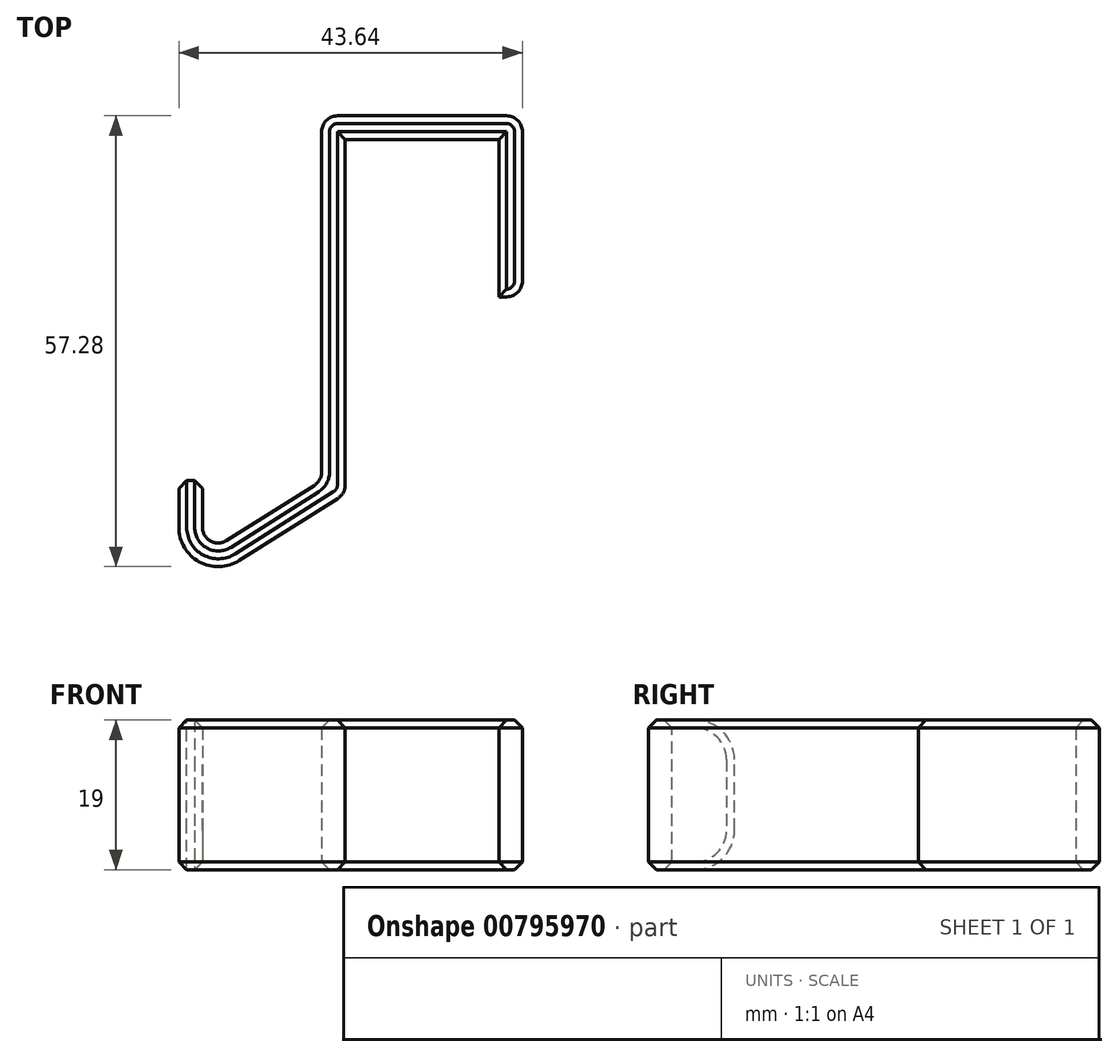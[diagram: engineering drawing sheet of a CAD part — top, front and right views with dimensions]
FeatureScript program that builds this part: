
annotation { "Feature Type Name" : "Feature", "Feature Type Description" : "" }
export const myFeature = defineFeature(function(context is Context, id is Id, definition is map)
    precondition{}
    {
        {
            var Q0;
            Q0=qCreatedBy(makeId("Top.planeOp"),FACE);
            var sketch = newSketch(context, id + "F0", { "sketchPlane" : qUnion([Q0])});
            skLineSegment(sketch, "E0", {"start": v(0, 0) * mm, "end": v(0, -15) * mm});
            skLineSegment(sketch, "E1", {"start": v(0, -15) * mm, "end": v(21.14, -1.65) * mm});
            skLineSegment(sketch, "E2", {"start": v(21.14, -1.65) * mm, "end": v(21.14, 43.35) * mm});
            skLineSegment(sketch, "E3", {"start": v(21.14, 43.35) * mm, "end": v(40.64, 43.35) * mm});
            skLineSegment(sketch, "E4", {"start": v(40.64, 43.35) * mm, "end": v(40.64, 23.35) * mm});
            skLineSegment(sketch, "E5", {"start": v(40.64, 23.35) * mm, "end": v(43.64, 23.35) * mm});
            skLineSegment(sketch, "E6", {"start": v(43.64, 23.35) * mm, "end": v(43.64, 46.35) * mm});
            skLineSegment(sketch, "E7", {"start": v(43.64, 46.35) * mm, "end": v(18.14, 46.35) * mm});
            skLineSegment(sketch, "E8", {"start": v(18.14, 46.35) * mm, "end": v(18.14, 0) * mm});
            skLineSegment(sketch, "E9", {"start": v(18.14, 0) * mm, "end": v(3, -9.56) * mm});
            skLineSegment(sketch, "E10", {"start": v(3, -9.56) * mm, "end": v(3, 0) * mm});
            skLineSegment(sketch, "E11", {"start": v(3, 0) * mm, "end": v(0, 0) * mm});
            skSolve(sketch);
        }
        {
            var Q0;
            Q0=makeQuery(id+"F0.imprint","IMPRINT",FACE,{"disambiguationData":[TD([[makeQuery(id+"F0.imprint","IMPRINT",EDGE,{"derivedFrom":sQuery(id+"F0.wireOp",EDGE,"E0")}),1.0]])]});
            extrude(context, id + "F1", {"entities" : qUnion([Q0]), "depth" : 19 * mm, "offsetDistance" : 25 * mm});
        }
        {
            var Q0;
            Q0=makeQuery(id+"F1.opExtrude","CAP_EDGE",EDGE,{"disambiguationData":[OSD([sQuery(id+"F0.wireOp",EDGE,"E11")])],"isStart":true});
            var Q1;
            Q1=makeQuery(id+"F1.opExtrude","CAP_EDGE",EDGE,{"disambiguationData":[OSD([sQuery(id+"F0.wireOp",EDGE,"E11")])],"isStart":false});
            fillet(context, id + "F2", {"entities" : qUnion([Q0, Q1]), "radius" : 5 * mm, "tangentPropagation" : true, "allowEdgeOverflow" : false});
        }
        {
            var Q0;
            Q0=makeQuery(id+"F1.opExtrude","SWEPT_EDGE",EDGE,{"disambiguationData":[OSD([sQuery(id+"F0.wireOp",EDGE,"E7"),sQuery(id+"F0.wireOp",EDGE,"E8")])]});
            var Q1;
            Q1=makeQuery(id+"F1.opExtrude","SWEPT_EDGE",EDGE,{"disambiguationData":[OSD([sQuery(id+"F0.wireOp",EDGE,"E9"),sQuery(id+"F0.wireOp",EDGE,"E10")])]});
            var Q2;
            Q2=makeQuery(id+"F1.opExtrude","SWEPT_EDGE",EDGE,{"disambiguationData":[OSD([sQuery(id+"F0.wireOp",EDGE,"E5"),sQuery(id+"F0.wireOp",EDGE,"E6")])]});
            var Q3;
            Q3=makeQuery(id+"F1.opExtrude","SWEPT_EDGE",EDGE,{"disambiguationData":[OSD([sQuery(id+"F0.wireOp",EDGE,"E8"),sQuery(id+"F0.wireOp",EDGE,"E9")])]});
            var Q4;
            Q4=makeQuery(id+"F1.opExtrude","SWEPT_EDGE",EDGE,{"disambiguationData":[OSD([sQuery(id+"F0.wireOp",EDGE,"E1"),sQuery(id+"F0.wireOp",EDGE,"E2")])]});
            var Q5;
            Q5=makeQuery(id+"F1.opExtrude","SWEPT_EDGE",EDGE,{"disambiguationData":[OSD([sQuery(id+"F0.wireOp",EDGE,"E6"),sQuery(id+"F0.wireOp",EDGE,"E7")])]});
            fillet(context, id + "F3", {"entities" : qUnion([Q0, Q1, Q2, Q3, Q4, Q5]), "radius" : 2 * mm, "tangentPropagation" : true, "allowEdgeOverflow" : false});
        }
        {
            var Q0;
            Q0=makeQuery(id+"F1.opExtrude","SWEPT_EDGE",EDGE,{"disambiguationData":[OSD([sQuery(id+"F0.wireOp",EDGE,"E0"),sQuery(id+"F0.wireOp",EDGE,"E1")])]});
            fillet(context, id + "F4", {"entities" : qUnion([Q0]), "radius" : 5 * mm, "tangentPropagation" : true, "allowEdgeOverflow" : false});
        }
        {
            var Q0;
            Q0=makeQuery(id+"F1.opExtrude","CAP_EDGE",EDGE,{"disambiguationData":[OSD([sQuery(id+"F0.wireOp",EDGE,"E1")])],"isStart":false});
            var Q1;
            Q1=makeQuery(id+"F1.opExtrude","CAP_EDGE",EDGE,{"disambiguationData":[OSD([sQuery(id+"F0.wireOp",EDGE,"E9")])],"isStart":false});
            var Q2;
            Q2=makeQuery(id+"F1.opExtrude","CAP_EDGE",EDGE,{"disambiguationData":[OSD([sQuery(id+"F0.wireOp",EDGE,"E3")])],"isStart":true});
            var Q3;
            Q3=makeQuery(id+"F1.opExtrude","CAP_EDGE",EDGE,{"disambiguationData":[OSD([sQuery(id+"F0.wireOp",EDGE,"E4")])],"isStart":true});
            var Q4;
            Q4=makeQuery(id+"F1.opExtrude","CAP_EDGE",EDGE,{"disambiguationData":[OSD([sQuery(id+"F0.wireOp",EDGE,"E3")])],"isStart":false});
            var Q5;
            Q5=makeQuery(id+"F1.opExtrude","CAP_EDGE",EDGE,{"disambiguationData":[OSD([sQuery(id+"F0.wireOp",EDGE,"E4")])],"isStart":false});
            chamfer(context, id + "F5", {"entities" : qUnion([Q0, Q1, Q2, Q3, Q4, Q5]), "width" : 1 * mm, "tangentPropagation" : true});
        }
    });
